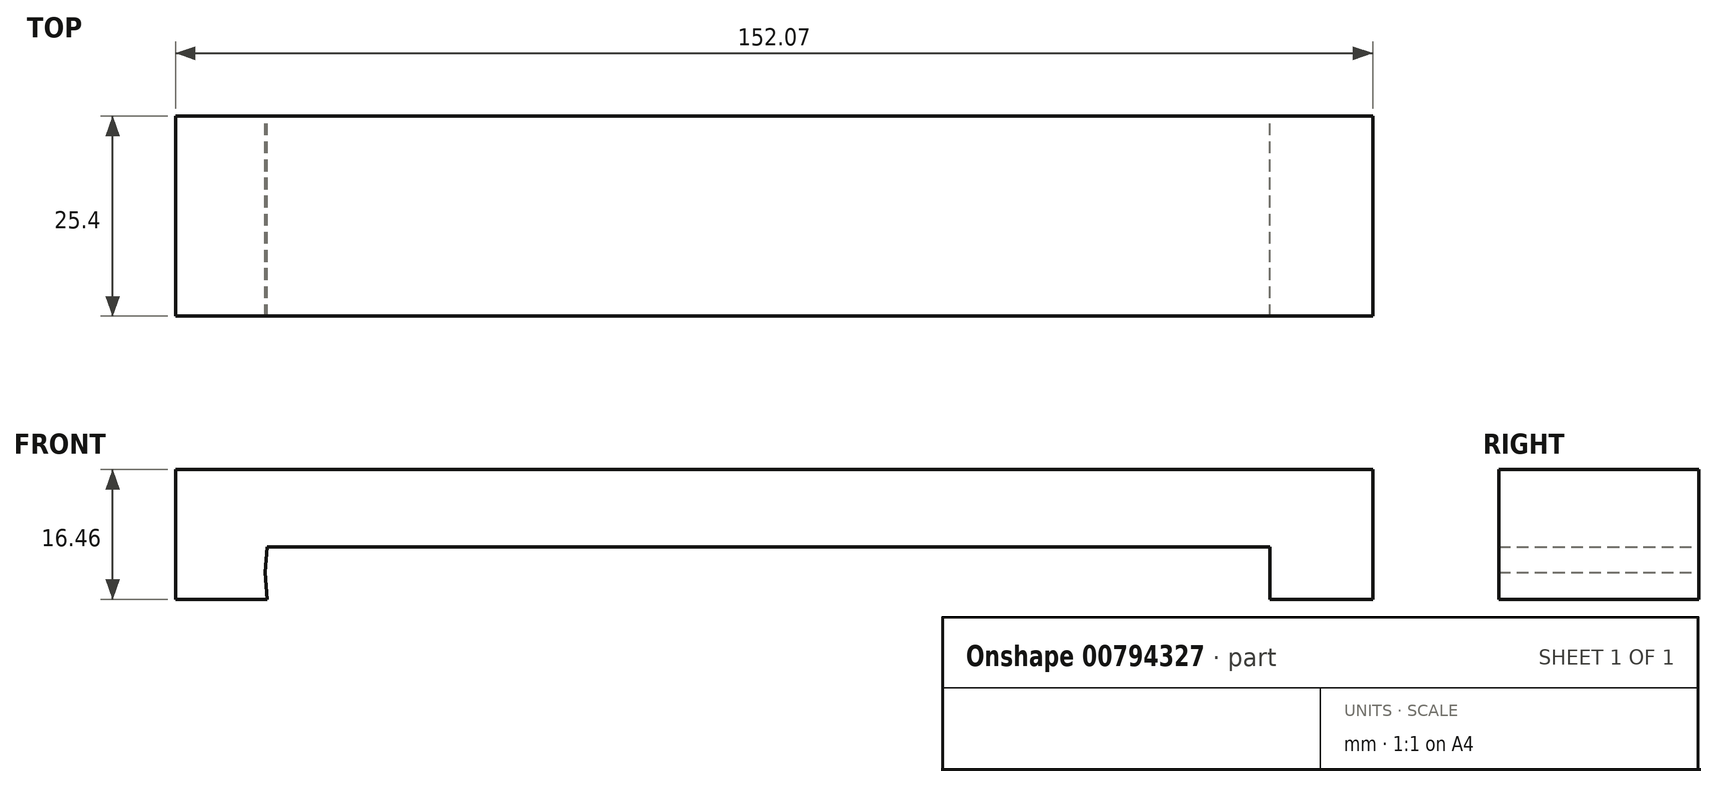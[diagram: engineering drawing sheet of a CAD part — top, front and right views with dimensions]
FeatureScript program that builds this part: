
annotation { "Feature Type Name" : "Feature", "Feature Type Description" : "" }
export const myFeature = defineFeature(function(context is Context, id is Id, definition is map)
    precondition{}
    {
        {
            var Q0;
            Q0=qCreatedBy(makeId("Front.planeOp"),FACE);
            var sketch = newSketch(context, id + "F0", { "sketchPlane" : qUnion([Q0])});
            skLineSegment(sketch, "E0", {"start": v(-76.46, 0) * mm, "end": v(-76.46, 9.79) * mm});
            skLineSegment(sketch, "E1", {"start": v(-76.46, 9.79) * mm, "end": v(75.61, 9.79) * mm});
            skLineSegment(sketch, "E2", {"start": v(75.61, 9.79) * mm, "end": v(75.61, -3.26) * mm});
            skLineSegment(sketch, "E3", {"start": v(-76.46, 0) * mm, "end": v(-76.46, -6.67) * mm});
            skLineSegment(sketch, "E4", {"start": v(-76.46, -6.67) * mm, "end": v(-64.83, -6.67) * mm});
            skLineSegment(sketch, "E5", {"start": v(-65.11, -3.26) * mm, "end": v(-64.83, 0) * mm});
            skLineSegment(sketch, "E6", {"start": v(-64.83, 0) * mm, "end": v(62.56, 0) * mm});
            skLineSegment(sketch, "E7", {"start": v(62.56, 0) * mm, "end": v(62.56, -6.67) * mm});
            skLineSegment(sketch, "E8", {"start": v(62.56, -6.67) * mm, "end": v(75.61, -6.67) * mm});
            skLineSegment(sketch, "E9", {"start": v(75.61, -6.67) * mm, "end": v(75.61, 0) * mm});
            skLineSegment(sketch, "E10", {"start": v(-64.83, -6.67) * mm, "end": v(-65.11, -3.26) * mm});
            skSolve(sketch);
        }
        {
            var Q0;
            Q0 = qSketchRegion(id + "F0", true);
            extrude(context, id + "F1", {"entities" : qUnion([Q0]), "depth" : 25.4 * mm, "offsetDistance" : 25.4 * mm});
        }
    });
